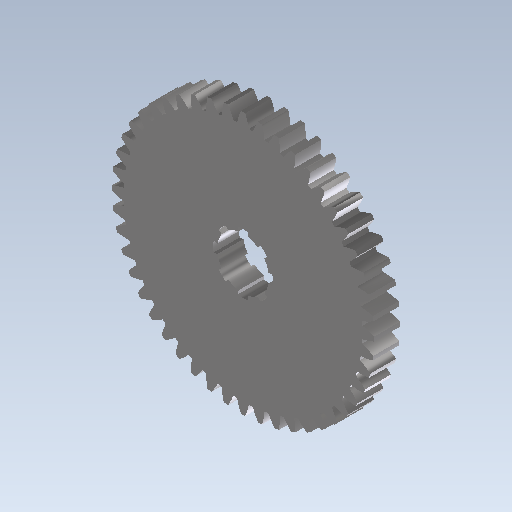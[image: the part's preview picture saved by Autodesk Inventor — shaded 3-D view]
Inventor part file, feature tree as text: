
AUTODESK INVENTOR PART (.ipt)
format: ipt  version: 2020 (Build 240168000, 168)  size: 385,536 bytes
history: native  units: mm (DEFAULTED — no unit token found)
features: extrude x3, plane x3, other x3, sketch x3, pattern_circular x1
ambient origin geometry x8: Origin, YZ Plane, XZ Plane, XY Plane, X Axis, Y Axis, Z Axis, Center Point
bodies: Solid1 (feature_tree)
feature tree (13):
  extrude  "Extrusion1"  Depth=1.0mm TaperAngle=0.0deg
  plane  "Work Plane2"
  plane  "Work Plane8"
  plane  "Work Plane9"
  other  "Цилиндрическое зубчатое зацепление"
  extrude  "Выдавливание2"  Depth=1.0mm
  extrude  "Выдавливание3"  Depth=10.0mm TaperAngle=0.0deg
  pattern_circular  "Круговой массив1"  [2 undecoded]
  sketch  "Sketch2"  dims[d0=10.116mm d1=1.0mm d2=0.0mm d3=9.762712mm d4=10.0mm d5=0.0mm d16=6.0mm d17=0.0mm d34=0.654498mm d39=0.0mm d41=0.0mm d43=6.0mm d46=6.0mm d47=0.0mm d48=0.0mm d49=2.0mm d50=10.0mm d51=0.0mm d52=2.3mm d53=3.490659mm d54=1.0mm d55=0.0mm d56=80.0mm d57=360.0deg]
  other  "Srf1"
  sketch  "Эскиз3"
  sketch  "Эскиз4"
  other  "Средний диаметр"
note: 2 required parameter values undecoded (feature->parameter linkage not recoverable at this tier; creation-order binding heuristic only, values carry confidence <= 0.55)
